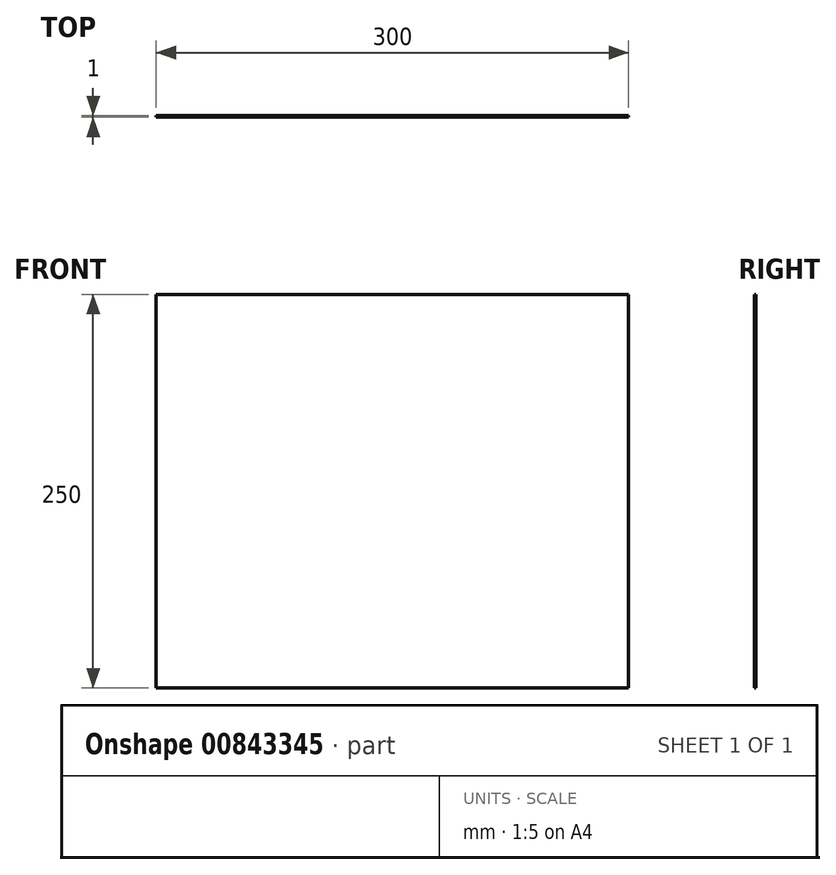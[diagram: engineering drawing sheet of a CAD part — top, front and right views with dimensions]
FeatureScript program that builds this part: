
annotation { "Feature Type Name" : "Feature", "Feature Type Description" : "" }
export const myFeature = defineFeature(function(context is Context, id is Id, definition is map)
    precondition{}
    {
        {
            var Q0;
            Q0=qCreatedBy(makeId("Front.planeOp"),FACE);
            var sketch = newSketch(context, id + "F0", { "sketchPlane" : qUnion([Q0])});
            skLineSegment(sketch, "E0.bottom", {"start": v(150, 125) * mm, "end": v(-150, 125) * mm});
            skLineSegment(sketch, "E0.top", {"start": v(150, -125) * mm, "end": v(-150, -125) * mm});
            skLineSegment(sketch, "E0.left", {"start": v(150, 125) * mm, "end": v(150, -125) * mm});
            skLineSegment(sketch, "E0.right", {"start": v(-150, 125) * mm, "end": v(-150, -125) * mm});
            skPoint(sketch, "E0.middle", {"position": v(0, 0) * mm});
            skSolve(sketch);
        }
        {
            var Q0;
            Q0 = qSketchRegion(id + "F0", true);
            extrude(context, id + "F1", {"entities" : qUnion([Q0]), "depth" : 1 * mm, "offsetDistance" : 25 * mm});
        }
    });
